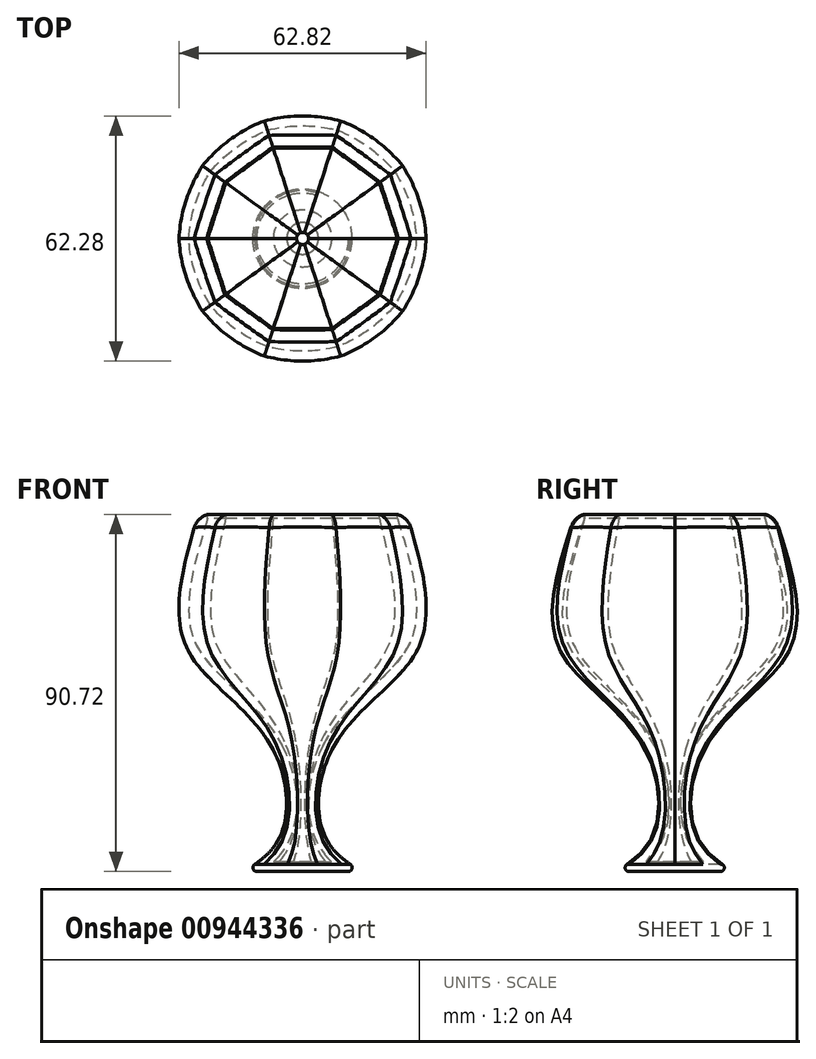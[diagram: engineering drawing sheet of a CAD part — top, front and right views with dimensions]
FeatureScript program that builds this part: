
annotation { "Feature Type Name" : "Feature", "Feature Type Description" : "" }
export const myFeature = defineFeature(function(context is Context, id is Id, definition is map)
    precondition{}
    {
        {
            var Q0;
            Q0=qCreatedBy(makeId("Top.planeOp"),FACE);
            cPlane(context, id + "F0", {"entities" : qUnion([Q0]), "cplaneType" : CPlaneType.OFFSET, "offset" : 85 * mm, "width" : 150 * mm, "height" : 150 * mm});
        }
        {
            var Q0;
            Q0=qCreatedBy(makeId("Top.planeOp"),FACE);
            var sketch = newSketch(context, id + "F1", { "sketchPlane" : qUnion([Q0])});
            skCircle(sketch, "E0", {"center": v(0, 0) * mm, "radius": 7.5 * mm});
            skSolve(sketch);
        }
        {
            var Q0;
            Q0=qCreatedBy(makeId("Top.planeOp"),FACE);
            cPlane(context, id + "F2", {"entities" : qUnion([Q0]), "cplaneType" : CPlaneType.OFFSET, "offset" : 51.1 * mm, "width" : 150 * mm, "height" : 150 * mm});
        }
        {
            var Q0;
            Q0=qCreatedBy(id+"F2.planeOp",FACE);
            var sketch = newSketch(context, id + "F3", { "sketchPlane" : qUnion([Q0])});
            skCircle(sketch, "E1", {"center": v(0, 0) * mm, "radius": 29.53 * mm});
            skSolve(sketch);
        }
        {
            var Q0;
            Q0=qCreatedBy(id+"F0.planeOp",FACE);
            var sketch = newSketch(context, id + "F4", { "sketchPlane" : qUnion([Q0])});
            skCircle(sketch, "E2.cCircle", {"center": v(0, 0) * mm, "radius": 26.48 * mm, "construction": true});
            skLineSegment(sketch, "E2.0", {"start": v(26.48, 0) * mm, "end": v(21.42, -15.56) * mm});
            skLineSegment(sketch, "E2.1", {"start": v(21.42, -15.56) * mm, "end": v(8.18, -25.18) * mm});
            skLineSegment(sketch, "E2.2", {"start": v(8.18, -25.18) * mm, "end": v(-8.18, -25.18) * mm});
            skLineSegment(sketch, "E2.3", {"start": v(-8.18, -25.18) * mm, "end": v(-21.42, -15.56) * mm});
            skLineSegment(sketch, "E2.4", {"start": v(-21.42, -15.56) * mm, "end": v(-26.48, 0) * mm});
            skLineSegment(sketch, "E2.5", {"start": v(-26.48, 0) * mm, "end": v(-21.42, 15.56) * mm});
            skLineSegment(sketch, "E2.6", {"start": v(-21.42, 15.56) * mm, "end": v(-8.18, 25.18) * mm});
            skLineSegment(sketch, "E2.7", {"start": v(-8.18, 25.18) * mm, "end": v(8.18, 25.18) * mm});
            skLineSegment(sketch, "E2.8", {"start": v(8.18, 25.18) * mm, "end": v(21.42, 15.56) * mm});
            skLineSegment(sketch, "E2.9", {"start": v(21.42, 15.56) * mm, "end": v(26.48, 0) * mm});
            skSolve(sketch);
        }
        {
            var Q0;
            Q0=qCreatedBy(makeId("Top.planeOp"),FACE);
            cPlane(context, id + "F5", {"entities" : qUnion([Q0]), "cplaneType" : CPlaneType.OFFSET, "offset" : 25 * mm, "width" : 150 * mm, "height" : 150 * mm});
        }
        {
            var Q0;
            Q0=qCreatedBy(id+"F5.planeOp",FACE);
            var sketch = newSketch(context, id + "F6", { "sketchPlane" : qUnion([Q0])});
            skCircle(sketch, "E3", {"center": v(0, 0) * mm, "radius": 7.5 * mm});
            skSolve(sketch);
        }
        {
            var Q0;
            Q0=qCreatedBy(makeId("Top.planeOp"),FACE);
            cPlane(context, id + "F7", {"entities" : qUnion([Q0]), "cplaneType" : CPlaneType.OFFSET, "offset" : 6 * mm, "oppositeDirection" : true, "width" : 150 * mm, "height" : 150 * mm});
        }
        {
            var Q0;
            Q0=qCreatedBy(id+"F7.planeOp",FACE);
            var sketch = newSketch(context, id + "F8", { "sketchPlane" : qUnion([Q0])});
            skCircle(sketch, "E4", {"center": v(0, 0) * mm, "radius": 14.88 * mm});
            skSolve(sketch);
        }
        {
            var Q0;
            Q0=makeQuery(id+"F4.imprint","IMPRINT",FACE,{"disambiguationData":[TD([[makeQuery(id+"F4.imprint","IMPRINT",EDGE,{"derivedFrom":sQuery(id+"F4.wireOp",EDGE,"E2.0")}),-1.0]])]});
            var Q1;
            Q1=makeQuery(id+"F3.imprint","IMPRINT",FACE,{"disambiguationData":[TD([[makeQuery(id+"F3.imprint","IMPRINT",EDGE,{"derivedFrom":sQuery(id+"F3.wireOp",EDGE,"E1")}),1.0]])]});
            var Q2;
            Q2=makeQuery(id+"F6.imprint","IMPRINT",FACE,{"disambiguationData":[TD([[makeQuery(id+"F6.imprint","IMPRINT",EDGE,{"derivedFrom":sQuery(id+"F6.wireOp",EDGE,"E3")}),1.0]])]});
            var Q3;
            Q3=makeQuery(id+"F1.imprint","IMPRINT",FACE,{"disambiguationData":[TD([[makeQuery(id+"F1.imprint","IMPRINT",EDGE,{"derivedFrom":sQuery(id+"F1.wireOp",EDGE,"E0")}),1.0]])]});
            var Q4;
            Q4=makeQuery(id+"F8.imprint","IMPRINT",FACE,{"disambiguationData":[TD([[makeQuery(id+"F8.imprint","IMPRINT",EDGE,{"derivedFrom":sQuery(id+"F8.wireOp",EDGE,"E4")}),1.0]])]});
            loft(context, id + "F9", {"sheetProfilesArray" : [{ "sheetProfileEntities" : qUnion([Q0]) }, { "sheetProfileEntities" : qUnion([Q1]) }, { "sheetProfileEntities" : qUnion([Q2]) }, { "sheetProfileEntities" : qUnion([Q3]) }, { "sheetProfileEntities" : qUnion([Q4]) }]});
        }
        {
            var Q0;
            Q0=makeQuery(id+"F9.opLoft","CAP_FACE",FACE,{"disambiguationData":[OSD([makeQuery(id+"F4.imprint","IMPRINT",FACE,{"disambiguationData":[TD([[makeQuery(id+"F4.imprint","IMPRINT",EDGE,{"derivedFrom":sQuery(id+"F4.wireOp",EDGE,"E2.0")}),-1.0]])]})])],"isStart":true});
            shell(context, id + "F10", {"entities" : qUnion([Q0]), "thickness" : 2.5 * mm});
        }
        {
            var Q0;
            Q0=makeQuery(id+"F10.opShell","OFFSET_EDGE",EDGE,{"disambiguationData":[OSD([sQuery(id+"F4.wireOp",EDGE,"E2.5"),sQuery(id+"F4.wireOp",EDGE,"E2.6"),sQuery(id+"F4.wireOp",EDGE,"E2.7")])]});
            var Q1;
            Q1=makeQuery(id+"F10.opShell","OFFSET_EDGE",EDGE,{"disambiguationData":[OSD([sQuery(id+"F4.wireOp",EDGE,"E2.4"),sQuery(id+"F4.wireOp",EDGE,"E2.5"),sQuery(id+"F4.wireOp",EDGE,"E2.6")])]});
            var Q2;
            Q2=makeQuery(id+"F10.opShell","OFFSET_EDGE",EDGE,{"disambiguationData":[OSD([sQuery(id+"F4.wireOp",EDGE,"E2.3"),sQuery(id+"F4.wireOp",EDGE,"E2.4"),sQuery(id+"F4.wireOp",EDGE,"E2.5")])]});
            var Q3;
            Q3=makeQuery(id+"F10.opShell","OFFSET_EDGE",EDGE,{"disambiguationData":[OSD([sQuery(id+"F4.wireOp",EDGE,"E2.2"),sQuery(id+"F4.wireOp",EDGE,"E2.3"),sQuery(id+"F4.wireOp",EDGE,"E2.4")])]});
            var Q4;
            Q4=makeQuery(id+"F10.opShell","OFFSET_EDGE",EDGE,{"disambiguationData":[OSD([sQuery(id+"F4.wireOp",EDGE,"E2.1"),sQuery(id+"F4.wireOp",EDGE,"E2.2"),sQuery(id+"F4.wireOp",EDGE,"E2.3")])]});
            var Q5;
            Q5=makeQuery(id+"F10.opShell","OFFSET_EDGE",EDGE,{"disambiguationData":[OSD([sQuery(id+"F4.wireOp",EDGE,"E2.0"),sQuery(id+"F4.wireOp",EDGE,"E2.1"),sQuery(id+"F4.wireOp",EDGE,"E2.2")])]});
            var Q6;
            Q6=makeQuery(id+"F10.opShell","OFFSET_EDGE",EDGE,{"disambiguationData":[OSD([sQuery(id+"F4.wireOp",EDGE,"E2.0"),sQuery(id+"F4.wireOp",EDGE,"E2.1"),sQuery(id+"F4.wireOp",EDGE,"E2.9")])]});
            var Q7;
            Q7=makeQuery(id+"F10.opShell","OFFSET_EDGE",EDGE,{"disambiguationData":[OSD([sQuery(id+"F4.wireOp",EDGE,"E2.0"),sQuery(id+"F4.wireOp",EDGE,"E2.8"),sQuery(id+"F4.wireOp",EDGE,"E2.9")])]});
            var Q8;
            Q8=makeQuery(id+"F10.opShell","OFFSET_EDGE",EDGE,{"disambiguationData":[OSD([sQuery(id+"F4.wireOp",EDGE,"E2.7"),sQuery(id+"F4.wireOp",EDGE,"E2.8"),sQuery(id+"F4.wireOp",EDGE,"E2.9")])]});
            var Q9;
            Q9=makeQuery(id+"F10.opShell","OFFSET_EDGE",EDGE,{"disambiguationData":[OSD([sQuery(id+"F4.wireOp",EDGE,"E2.6"),sQuery(id+"F4.wireOp",EDGE,"E2.7"),sQuery(id+"F4.wireOp",EDGE,"E2.8")])]});
            fillet(context, id + "F11", {"entities" : qUnion([Q0, Q1, Q2, Q3, Q4, Q5, Q6, Q7, Q8, Q9]), "radius" : 1 * mm, "tangentPropagation" : true, "allowEdgeOverflow" : false});
        }
        {
            var Q0;
            Q0=makeQuery(id+"F9.opLoft","MID_CAP_EDGE",EDGE,{"disambiguationData":[OSD([sQuery(id+"F4.wireOp",EDGE,"E2.2"),sQuery(id+"F4.wireOp",EDGE,"E2.3"),sQuery(id+"F4.wireOp",EDGE,"E2.4")])],"capPos":0.0});
            var Q1;
            Q1=makeQuery(id+"F9.opLoft","MID_CAP_EDGE",EDGE,{"disambiguationData":[OSD([sQuery(id+"F4.wireOp",EDGE,"E2.1"),sQuery(id+"F4.wireOp",EDGE,"E2.2"),sQuery(id+"F4.wireOp",EDGE,"E2.3")])],"capPos":0.0});
            var Q2;
            Q2=makeQuery(id+"F9.opLoft","MID_CAP_EDGE",EDGE,{"disambiguationData":[OSD([sQuery(id+"F4.wireOp",EDGE,"E2.0"),sQuery(id+"F4.wireOp",EDGE,"E2.1"),sQuery(id+"F4.wireOp",EDGE,"E2.2")])],"capPos":0.0});
            var Q3;
            Q3=makeQuery(id+"F9.opLoft","MID_CAP_EDGE",EDGE,{"disambiguationData":[OSD([sQuery(id+"F4.wireOp",EDGE,"E2.0"),sQuery(id+"F4.wireOp",EDGE,"E2.1"),sQuery(id+"F4.wireOp",EDGE,"E2.9")])],"capPos":0.0});
            var Q4;
            Q4=makeQuery(id+"F9.opLoft","MID_CAP_EDGE",EDGE,{"disambiguationData":[OSD([sQuery(id+"F4.wireOp",EDGE,"E2.0"),sQuery(id+"F4.wireOp",EDGE,"E2.8"),sQuery(id+"F4.wireOp",EDGE,"E2.9")])],"capPos":0.0});
            var Q5;
            Q5=makeQuery(id+"F9.opLoft","MID_CAP_EDGE",EDGE,{"disambiguationData":[OSD([sQuery(id+"F4.wireOp",EDGE,"E2.7"),sQuery(id+"F4.wireOp",EDGE,"E2.8"),sQuery(id+"F4.wireOp",EDGE,"E2.9")])],"capPos":0.0});
            var Q6;
            Q6=makeQuery(id+"F9.opLoft","MID_CAP_EDGE",EDGE,{"disambiguationData":[OSD([sQuery(id+"F4.wireOp",EDGE,"E2.6"),sQuery(id+"F4.wireOp",EDGE,"E2.7"),sQuery(id+"F4.wireOp",EDGE,"E2.8")])],"capPos":0.0});
            var Q7;
            Q7=makeQuery(id+"F9.opLoft","MID_CAP_EDGE",EDGE,{"disambiguationData":[OSD([sQuery(id+"F4.wireOp",EDGE,"E2.5"),sQuery(id+"F4.wireOp",EDGE,"E2.6"),sQuery(id+"F4.wireOp",EDGE,"E2.7")])],"capPos":0.0});
            var Q8;
            Q8=makeQuery(id+"F9.opLoft","MID_CAP_EDGE",EDGE,{"disambiguationData":[OSD([sQuery(id+"F4.wireOp",EDGE,"E2.4"),sQuery(id+"F4.wireOp",EDGE,"E2.5"),sQuery(id+"F4.wireOp",EDGE,"E2.6")])],"capPos":0.0});
            var Q9;
            Q9=makeQuery(id+"F9.opLoft","MID_CAP_EDGE",EDGE,{"disambiguationData":[OSD([sQuery(id+"F4.wireOp",EDGE,"E2.3"),sQuery(id+"F4.wireOp",EDGE,"E2.4"),sQuery(id+"F4.wireOp",EDGE,"E2.5")])],"capPos":0.0});
            fillet(context, id + "F12", {"entities" : qUnion([Q0, Q1, Q2, Q3, Q4, Q5, Q6, Q7, Q8, Q9]), "radius" : 5 * mm, "tangentPropagation" : true, "allowEdgeOverflow" : false});
        }
        {
            var Q0;
            Q0=makeQuery(id+"F9.opLoft","MID_CAP_EDGE",EDGE,{"disambiguationData":[OSD([sQuery(id+"F4.wireOp",EDGE,"E2.0"),sQuery(id+"F4.wireOp",EDGE,"E2.1"),sQuery(id+"F4.wireOp",EDGE,"E2.9"),sQuery(id+"F8.wireOp",EDGE,"E4")])],"capPos":4.0});
            var Q1;
            Q1=makeQuery(id+"F9.opLoft","MID_CAP_EDGE",EDGE,{"disambiguationData":[OSD([sQuery(id+"F4.wireOp",EDGE,"E2.0"),sQuery(id+"F4.wireOp",EDGE,"E2.1"),sQuery(id+"F4.wireOp",EDGE,"E2.2"),sQuery(id+"F8.wireOp",EDGE,"E4")])],"capPos":4.0});
            var Q2;
            Q2=makeQuery(id+"F9.opLoft","MID_CAP_EDGE",EDGE,{"disambiguationData":[OSD([sQuery(id+"F4.wireOp",EDGE,"E2.1"),sQuery(id+"F4.wireOp",EDGE,"E2.2"),sQuery(id+"F4.wireOp",EDGE,"E2.3"),sQuery(id+"F8.wireOp",EDGE,"E4")])],"capPos":4.0});
            var Q3;
            Q3=makeQuery(id+"F9.opLoft","MID_CAP_EDGE",EDGE,{"disambiguationData":[OSD([sQuery(id+"F4.wireOp",EDGE,"E2.2"),sQuery(id+"F4.wireOp",EDGE,"E2.3"),sQuery(id+"F4.wireOp",EDGE,"E2.4"),sQuery(id+"F8.wireOp",EDGE,"E4")])],"capPos":4.0});
            var Q4;
            Q4=makeQuery(id+"F9.opLoft","MID_CAP_EDGE",EDGE,{"disambiguationData":[OSD([sQuery(id+"F4.wireOp",EDGE,"E2.3"),sQuery(id+"F4.wireOp",EDGE,"E2.4"),sQuery(id+"F4.wireOp",EDGE,"E2.5"),sQuery(id+"F8.wireOp",EDGE,"E4")])],"capPos":4.0});
            var Q5;
            Q5=makeQuery(id+"F9.opLoft","MID_CAP_EDGE",EDGE,{"disambiguationData":[OSD([sQuery(id+"F4.wireOp",EDGE,"E2.4"),sQuery(id+"F4.wireOp",EDGE,"E2.5"),sQuery(id+"F4.wireOp",EDGE,"E2.6"),sQuery(id+"F8.wireOp",EDGE,"E4")])],"capPos":4.0});
            var Q6;
            Q6=makeQuery(id+"F9.opLoft","MID_CAP_EDGE",EDGE,{"disambiguationData":[OSD([sQuery(id+"F4.wireOp",EDGE,"E2.5"),sQuery(id+"F4.wireOp",EDGE,"E2.6"),sQuery(id+"F4.wireOp",EDGE,"E2.7"),sQuery(id+"F8.wireOp",EDGE,"E4")])],"capPos":4.0});
            var Q7;
            Q7=makeQuery(id+"F9.opLoft","MID_CAP_EDGE",EDGE,{"disambiguationData":[OSD([sQuery(id+"F4.wireOp",EDGE,"E2.6"),sQuery(id+"F4.wireOp",EDGE,"E2.7"),sQuery(id+"F4.wireOp",EDGE,"E2.8"),sQuery(id+"F8.wireOp",EDGE,"E4")])],"capPos":4.0});
            var Q8;
            Q8=makeQuery(id+"F9.opLoft","MID_CAP_EDGE",EDGE,{"disambiguationData":[OSD([sQuery(id+"F4.wireOp",EDGE,"E2.0"),sQuery(id+"F4.wireOp",EDGE,"E2.9"),sQuery(id+"F8.wireOp",EDGE,"E4")])],"capPos":4.0});
            var Q9;
            Q9=makeQuery(id+"F9.opLoft","MID_CAP_EDGE",EDGE,{"disambiguationData":[OSD([sQuery(id+"F4.wireOp",EDGE,"E2.0"),sQuery(id+"F4.wireOp",EDGE,"E2.7"),sQuery(id+"F4.wireOp",EDGE,"E2.8"),sQuery(id+"F4.wireOp",EDGE,"E2.9"),sQuery(id+"F8.wireOp",EDGE,"E4")])],"capPos":4.0});
            fillet(context, id + "F13", {"entities" : qUnion([Q0, Q1, Q2, Q3, Q4, Q5, Q6, Q7, Q8, Q9]), "radius" : 1 * mm, "tangentPropagation" : true, "allowEdgeOverflow" : false});
        }
    });
